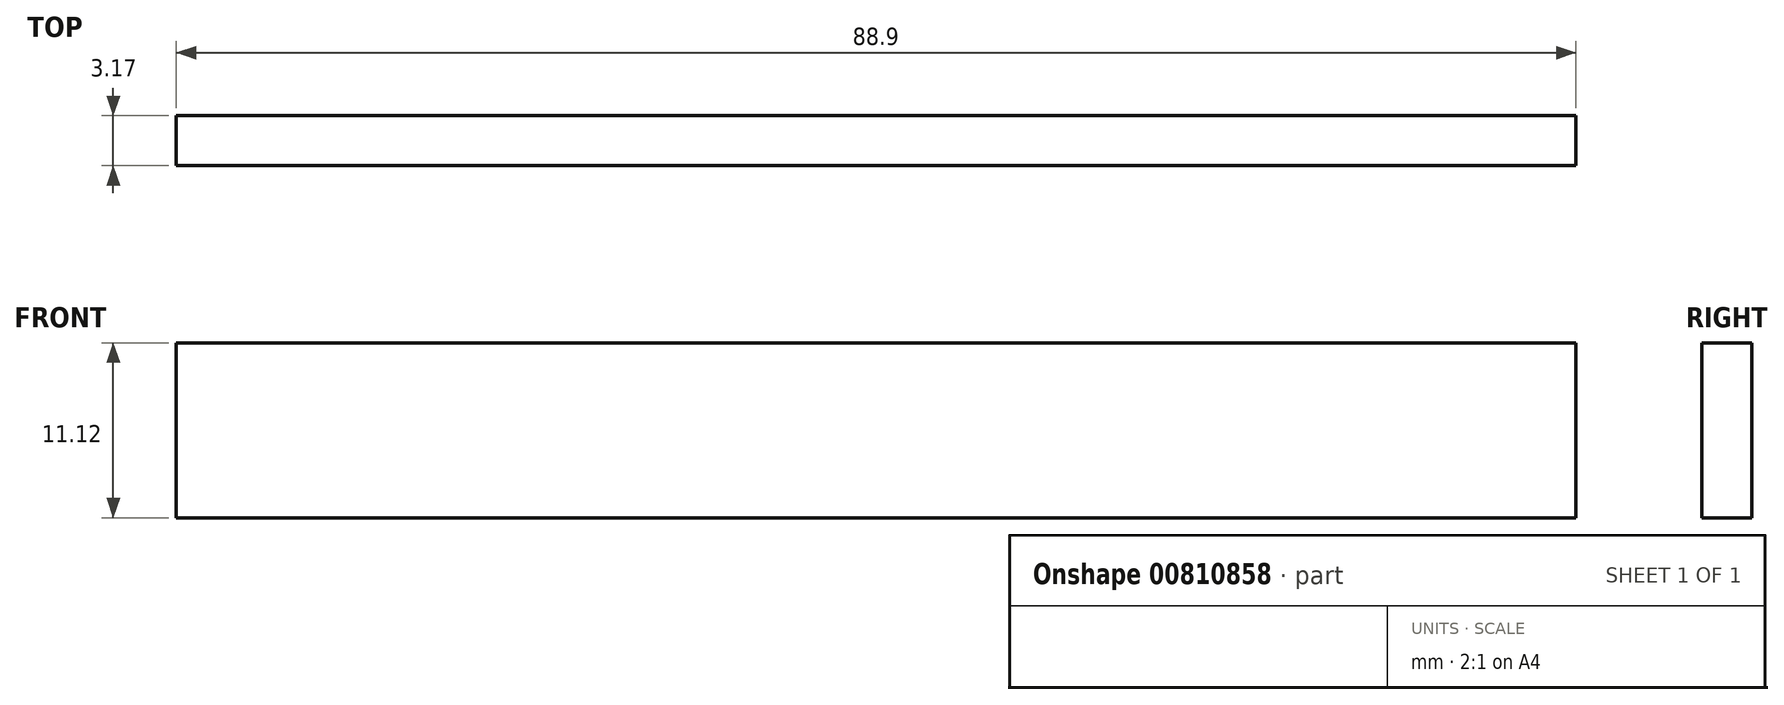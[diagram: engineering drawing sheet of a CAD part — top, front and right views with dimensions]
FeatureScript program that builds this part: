
annotation { "Feature Type Name" : "Feature", "Feature Type Description" : "" }
export const myFeature = defineFeature(function(context is Context, id is Id, definition is map)
    precondition{}
    {
        {
            var Q0;
            Q0=qCreatedBy(makeId("Front.planeOp"),FACE);
            var sketch = newSketch(context, id + "F0", { "sketchPlane" : qUnion([Q0])});
            skLineSegment(sketch, "E0.bottom", {"start": v(44.45, 5.56) * mm, "end": v(-44.45, 5.56) * mm});
            skLineSegment(sketch, "E0.top", {"start": v(44.45, -5.56) * mm, "end": v(-44.45, -5.56) * mm});
            skLineSegment(sketch, "E0.left", {"start": v(44.45, 5.56) * mm, "end": v(44.45, -5.56) * mm});
            skLineSegment(sketch, "E0.right", {"start": v(-44.45, 5.56) * mm, "end": v(-44.45, -5.56) * mm});
            skPoint(sketch, "E0.middle", {"position": v(0, 0) * mm});
            skSolve(sketch);
        }
        {
            var Q0;
            Q0=makeQuery(id+"F0.imprint","IMPRINT",FACE,{"disambiguationData":[TD([[makeQuery(id+"F0.imprint","IMPRINT",EDGE,{"derivedFrom":sQuery(id+"F0.wireOp",EDGE,"E0.bottom")}),1.0]])]});
            extrude(context, id + "F1", {"entities" : qUnion([Q0]), "depth" : 3.17 * mm, "offsetDistance" : 25.4 * mm});
        }
    });
